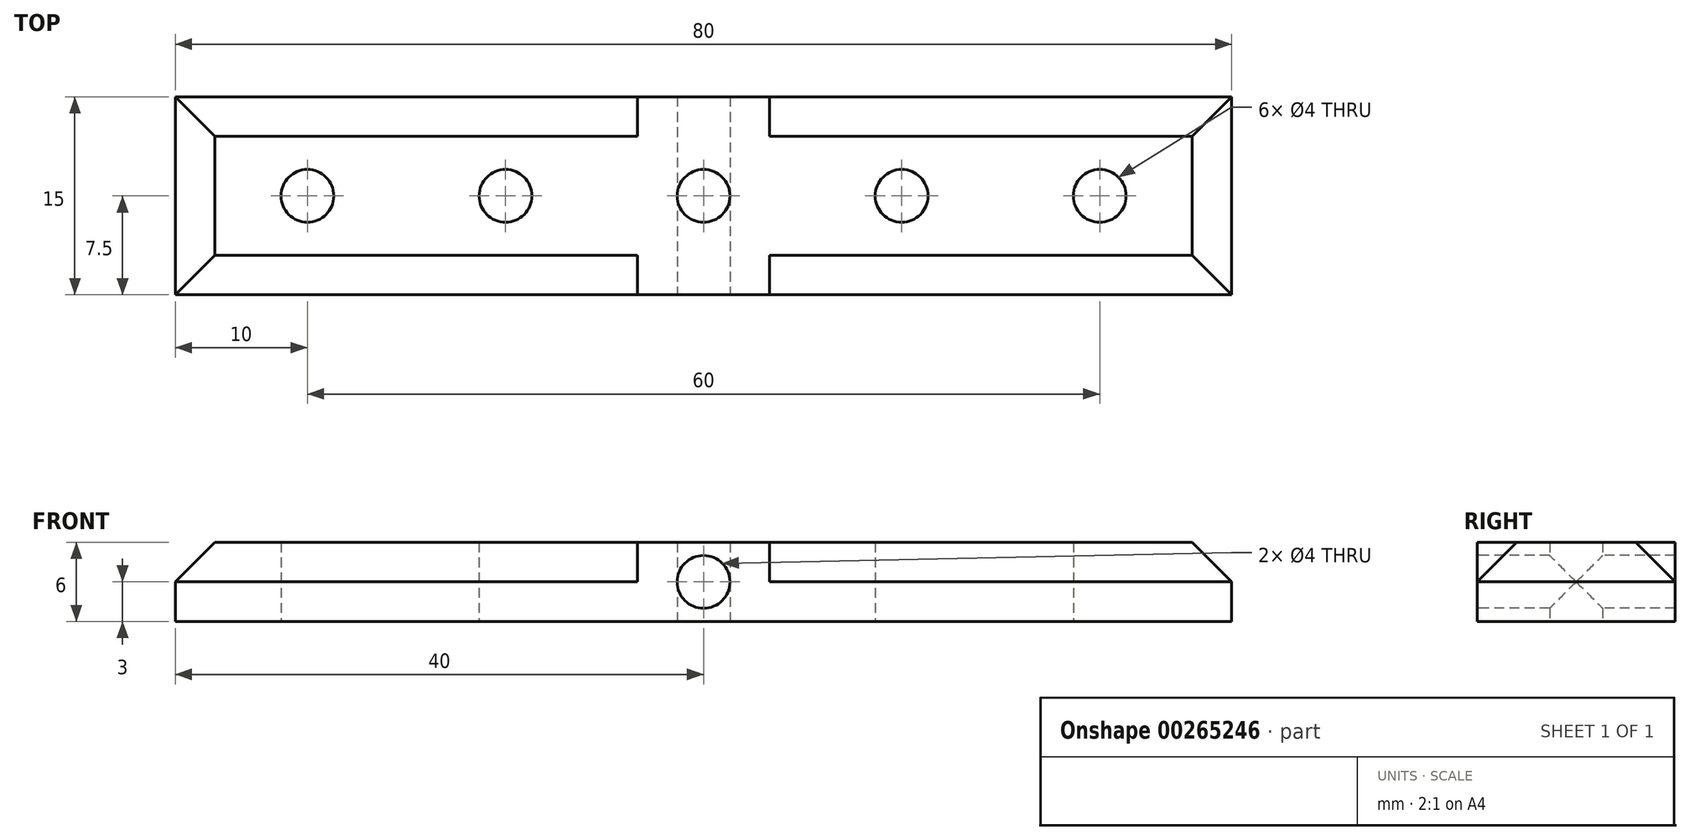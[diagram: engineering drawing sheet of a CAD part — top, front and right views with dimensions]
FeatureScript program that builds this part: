
annotation { "Feature Type Name" : "Feature", "Feature Type Description" : "" }
export const myFeature = defineFeature(function(context is Context, id is Id, definition is map)
    precondition{}
    {
        {
            var Q0;
            Q0=qCreatedBy(makeId("Top.planeOp"),FACE);
            var sketch = newSketch(context, id + "F0", { "sketchPlane" : qUnion([Q0])});
            skLineSegment(sketch, "E0.bottom", {"start": v(40, -7.5) * mm, "end": v(-40, -7.5) * mm});
            skLineSegment(sketch, "E0.top", {"start": v(40, 7.5) * mm, "end": v(-40, 7.5) * mm});
            skLineSegment(sketch, "E0.left", {"start": v(40, -7.5) * mm, "end": v(40, 7.5) * mm});
            skLineSegment(sketch, "E0.right", {"start": v(-40, -7.5) * mm, "end": v(-40, 7.5) * mm});
            skPoint(sketch, "E0.middle", {"position": v(0, 0) * mm});
            skCircle(sketch, "E1", {"center": v(0, 0) * mm, "radius": 2 * mm});
            skLineSegment(sketch, "E2.bottom", {"start": v(5, -7.5) * mm, "end": v(-5, -7.5) * mm});
            skLineSegment(sketch, "E2.top", {"start": v(5, 7.5) * mm, "end": v(-5, 7.5) * mm});
            skLineSegment(sketch, "E2.left", {"start": v(5, -7.5) * mm, "end": v(5, 7.5) * mm});
            skLineSegment(sketch, "E2.right", {"start": v(-5, -7.5) * mm, "end": v(-5, 7.5) * mm});
            skSolve(sketch);
        }
        {
            var Q0;
            Q0 = qSketchRegion(id + "F0", true);
            extrude(context, id + "F1", {"entities" : qUnion([Q0]), "depth" : 6 * mm});
        }
        {
            var Q0;
            Q0=makeQuery(id+"F1.opExtrude","CAP_EDGE",EDGE,{"disambiguationData":[OSD([sQuery(id+"F0.wireOp",EDGE,"E0.bottom")])],"isStart":false});
            var Q1;
            Q1=makeQuery(id+"F1.opExtrude","CAP_EDGE",EDGE,{"disambiguationData":[OSD([sQuery(id+"F0.wireOp",EDGE,"E0.right")])],"isStart":false});
            var Q2;
            Q2=makeQuery(id+"F1.opExtrude","CAP_EDGE",EDGE,{"disambiguationData":[OSD([sQuery(id+"F0.wireOp",EDGE,"E0.left")])],"isStart":false});
            var Q3;
            Q3=makeQuery(id+"F1.opExtrude","CAP_EDGE",EDGE,{"disambiguationData":[OSD([sQuery(id+"F0.wireOp",EDGE,"E0.top")])],"isStart":false});
            chamfer(context, id + "F2", {"entities" : qUnion([Q0, Q1, Q2, Q3]), "width" : 3 * mm, "tangentPropagation" : true});
        }
        {
            var Q0;
            Q0=makeQuery(id+"F1.opExtrude","CAP_FACE",FACE,{"disambiguationData":[OSD([sQuery(id+"F0.wireOp",EDGE,"E0.bottom"),sQuery(id+"F0.wireOp",EDGE,"E0.top"),sQuery(id+"F0.wireOp",EDGE,"E0.left"),sQuery(id+"F0.wireOp",EDGE,"E0.right"),sQuery(id+"F0.wireOp",EDGE,"E1")])],"isStart":true});
            var sketch = newSketch(context, id + "F3", { "sketchPlane" : qUnion([Q0])});
            skCircle(sketch, "E3", {"center": v(-30, 0) * mm, "radius": 2 * mm});
            skCircle(sketch, "E4", {"center": v(-15, 0) * mm, "radius": 2 * mm});
            skLineSegment(sketch, "E5", {"start": v(0, 21.51) * mm, "end": v(0, -15.66) * mm, "construction": true});
            skCircle(sketch, "E6.MirrorC", {"center": v(15, 0) * mm, "radius": 2 * mm});
            skCircle(sketch, "E7.MirrorC", {"center": v(30, 0) * mm, "radius": 2 * mm});
            skSolve(sketch);
        }
        {
            var Q0;
            Q0 = qSketchRegion(id + "F3", true);
            extrude(context, id + "F4", {"entities" : qUnion([Q0]), "operationType" : NewBodyOperationType.REMOVE, "oppositeDirection" : true, "depth" : 12 * mm});
        }
        {
            var Q0;
            Q0=makeQuery(id+"F0.imprint","IMPRINT",FACE,{"disambiguationData":[TD([[makeQuery(id+"F0.imprint","IMPRINT",EDGE,{"derivedFrom":sQuery(id+"F0.wireOp",EDGE,"E1")}),-1.0]])]});
            extrude(context, id + "F5", {"entities" : qUnion([Q0]), "operationType" : NewBodyOperationType.ADD, "depth" : 6 * mm});
        }
        {
            var Q0;
            Q0=makeQuery(id+"F1.opExtrude","SWEPT_FACE",FACE,{"disambiguationData":[OSD([sQuery(id+"F0.wireOp",EDGE,"E0.bottom"),sQuery(id+"F0.wireOp",EDGE,"E2.bottom")])]});
            var sketch = newSketch(context, id + "F6", { "sketchPlane" : qUnion([Q0])});
            skCircle(sketch, "E8", {"center": v(0, 3) * mm, "radius": 2 * mm});
            skSolve(sketch);
        }
        {
            var Q0;
            Q0 = qSketchRegion(id + "F6", true);
            extrude(context, id + "F7", {"entities" : qUnion([Q0]), "operationType" : NewBodyOperationType.REMOVE, "endBound" : BoundingType.THROUGH_ALL, "oppositeDirection" : true, "depth" : 30 * mm});
        }
    });
